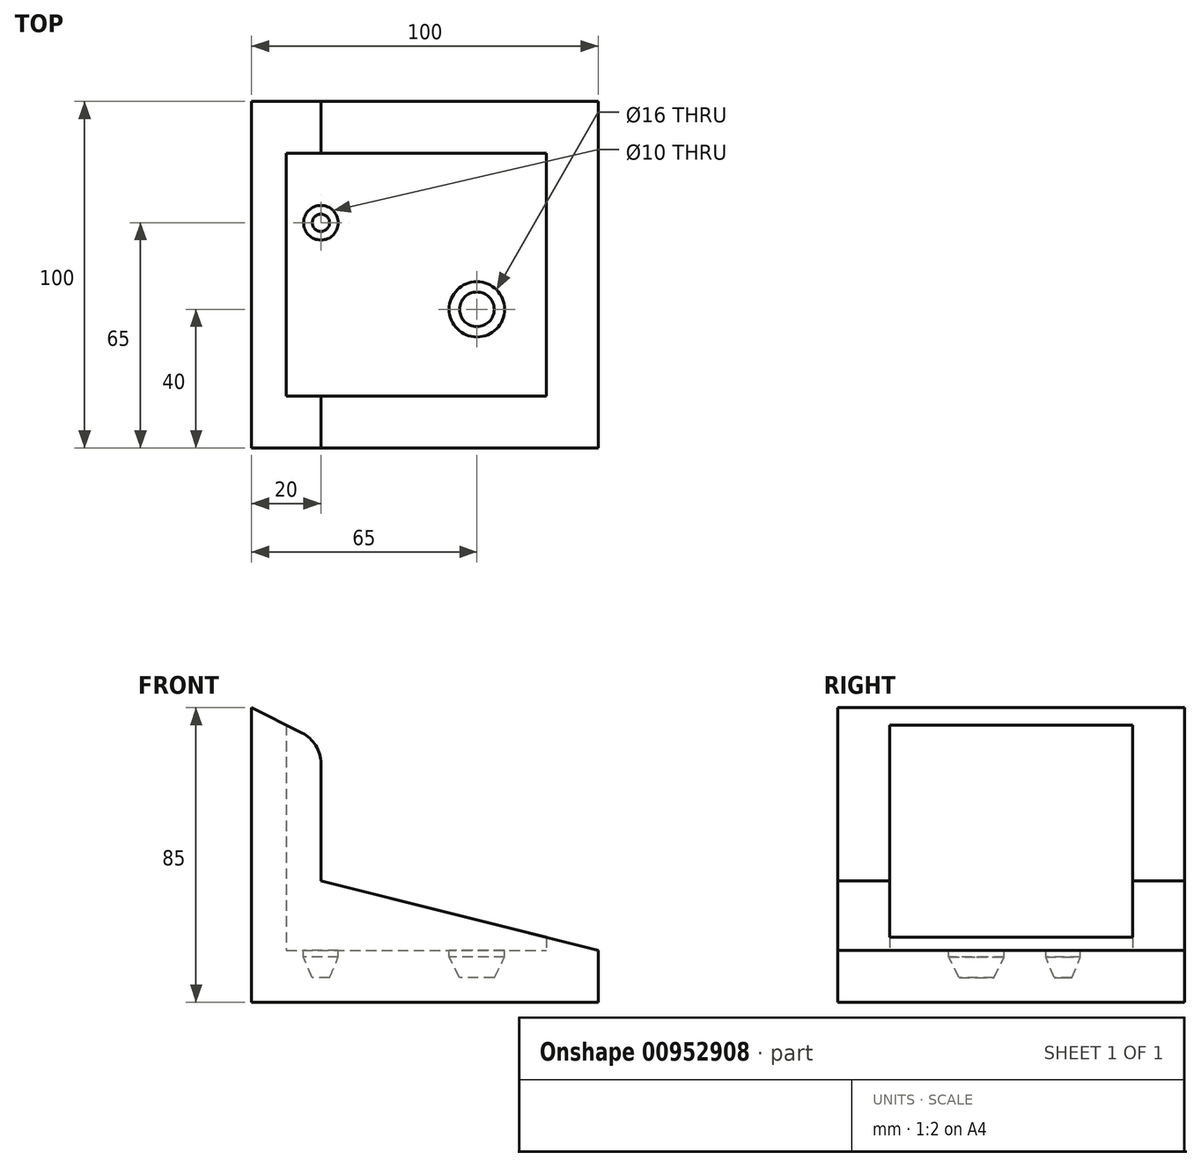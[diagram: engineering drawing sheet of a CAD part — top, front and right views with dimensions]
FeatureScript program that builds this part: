
annotation { "Feature Type Name" : "Feature", "Feature Type Description" : "" }
export const myFeature = defineFeature(function(context is Context, id is Id, definition is map)
    precondition{}
    {
        {
            var Q0;
            Q0=qCreatedBy(makeId("Front.planeOp"),FACE);
            var sketch = newSketch(context, id + "F0", { "sketchPlane" : qUnion([Q0])});
            skLineSegment(sketch, "E0", {"start": v(0, 0) * mm, "end": v(0, 85) * mm});
            skLineSegment(sketch, "E1", {"start": v(0, 85) * mm, "end": v(20, 75) * mm});
            skLineSegment(sketch, "E2", {"start": v(20, 75) * mm, "end": v(20, 35) * mm});
            skLineSegment(sketch, "E3", {"start": v(20, 35) * mm, "end": v(100, 15) * mm});
            skLineSegment(sketch, "E4", {"start": v(100, 15) * mm, "end": v(100, 0) * mm});
            skLineSegment(sketch, "E5", {"start": v(100, 0) * mm, "end": v(0, 0) * mm});
            skSolve(sketch);
        }
        {
            var Q0;
            Q0 = qSketchRegion(id + "F0", true);
            extrude(context, id + "F1", {"entities" : qUnion([Q0]), "oppositeDirection" : true, "depth" : 100 * mm, "offsetDistance" : 25 * mm});
        }
        {
            var Q0;
            Q0=makeQuery(id+"F1.opExtrude","SWEPT_EDGE",EDGE,{"disambiguationData":[OSD([sQuery(id+"F0.wireOp",EDGE,"E1"),sQuery(id+"F0.wireOp",EDGE,"E2")])]});
            fillet(context, id + "F2", {"entities" : qUnion([Q0]), "radius" : 9.9 * mm, "tangentPropagation" : true, "allowEdgeOverflow" : false});
        }
        {
            var Q0;
            Q0=makeQuery(id+"F1.opExtrude","SWEPT_FACE",FACE,{"disambiguationData":[OSD([sQuery(id+"F0.wireOp",EDGE,"E5")])]});
            cPlane(context, id + "F3", {"entities" : qUnion([Q0]), "cplaneType" : CPlaneType.OFFSET, "offset" : 15 * mm, "oppositeDirection" : true, "width" : 150 * mm, "height" : 150 * mm});
        }
        {
            var Q0;
            Q0=qCreatedBy(id+"F3.planeOp",FACE);
            var sketch = newSketch(context, id + "F4", { "sketchPlane" : qUnion([Q0])});
            skLineSegment(sketch, "E6.bottom", {"start": v(10, -85) * mm, "end": v(85, -85) * mm});
            skLineSegment(sketch, "E6.top", {"start": v(10, -15) * mm, "end": v(85, -15) * mm});
            skLineSegment(sketch, "E6.left", {"start": v(10, -85) * mm, "end": v(10, -15) * mm});
            skLineSegment(sketch, "E6.right", {"start": v(85, -85) * mm, "end": v(85, -15) * mm});
            skSolve(sketch);
        }
        {
            var Q0;
            Q0 = qSketchRegion(id + "F4", true);
            extrude(context, id + "F5", {"entities" : qUnion([Q0]), "operationType" : NewBodyOperationType.REMOVE, "endBound" : BoundingType.THROUGH_ALL, "oppositeDirection" : true, "depth" : 25 * mm, "offsetDistance" : 25 * mm});
        }
        {
            var Q0;
            Q0=makeQuery(id+"F5.boolean.opBoolean","COPY",FACE,{"derivedFrom":makeQuery(id+"F5.opExtrude","CAP_FACE",FACE,{"disambiguationData":[OSD([sQuery(id+"F4.wireOp",EDGE,"E6.bottom"),sQuery(id+"F4.wireOp",EDGE,"E6.top"),sQuery(id+"F4.wireOp",EDGE,"E6.left"),sQuery(id+"F4.wireOp",EDGE,"E6.right")])],"isStart":true})});
            var sketch = newSketch(context, id + "F6", { "sketchPlane" : qUnion([Q0])});
            skCircle(sketch, "E7", {"center": v(20, 65) * mm, "radius": 5 * mm});
            skCircle(sketch, "E8", {"center": v(65, 40) * mm, "radius": 8 * mm});
            skSolve(sketch);
        }
        {
            var Q0;
            Q0 = qSketchRegion(id + "F6", true);
            extrude(context, id + "F7", {"entities" : qUnion([Q0]), "operationType" : NewBodyOperationType.REMOVE, "oppositeDirection" : true, "depth" : 8 * mm, "offsetDistance" : 25 * mm});
        }
        {
            var Q0;
            Q0=makeQuery(id+"F1.opExtrude","SWEPT_FACE",FACE,{"disambiguationData":[OSD([sQuery(id+"F0.wireOp",EDGE,"E5")])]});
            cPlane(context, id + "F8", {"entities" : qUnion([Q0]), "cplaneType" : CPlaneType.OFFSET, "offset" : 7 * mm, "oppositeDirection" : true, "width" : 150 * mm, "height" : 150 * mm});
        }
        {
            var Q0;
            Q0=makeQuery(id+"F6.imprint","IMPRINT",FACE,{"disambiguationData":[TD([[makeQuery(id+"F6.imprint","IMPRINT",EDGE,{"derivedFrom":sQuery(id+"F6.wireOp",EDGE,"E7")}),-1.0]])]});
            cPlane(context, id + "F9", {"entities" : qUnion([Q0]), "cplaneType" : CPlaneType.OFFSET, "offset" : 2 * mm, "oppositeDirection" : true, "width" : 150 * mm, "height" : 150 * mm});
        }
        {
            var Q0;
            Q0=makeQuery(id+"F7.boolean.opBoolean","COPY",EDGE,{"derivedFrom":makeQuery(id+"F7.opExtrude","CAP_EDGE",EDGE,{"disambiguationData":[OSD([sQuery(id+"F6.wireOp",EDGE,"E7")])],"isStart":false})});
            chamfer(context, id + "F10", {"entities" : qUnion([Q0]), "chamferType" : ChamferType.TWO_OFFSETS, "width1" : 2.5 * mm, "oppositeDirection" : false, "width2" : 6 * mm, "tangentPropagation" : true});
        }
        {
            var Q0;
            Q0=makeQuery(id+"F7.boolean.opBoolean","COPY",EDGE,{"derivedFrom":makeQuery(id+"F7.opExtrude","CAP_EDGE",EDGE,{"disambiguationData":[OSD([sQuery(id+"F6.wireOp",EDGE,"E8")])],"isStart":false})});
            chamfer(context, id + "F11", {"entities" : qUnion([Q0]), "chamferType" : ChamferType.TWO_OFFSETS, "width1" : 3 * mm, "oppositeDirection" : false, "width2" : 6 * mm, "tangentPropagation" : true});
        }
    });
